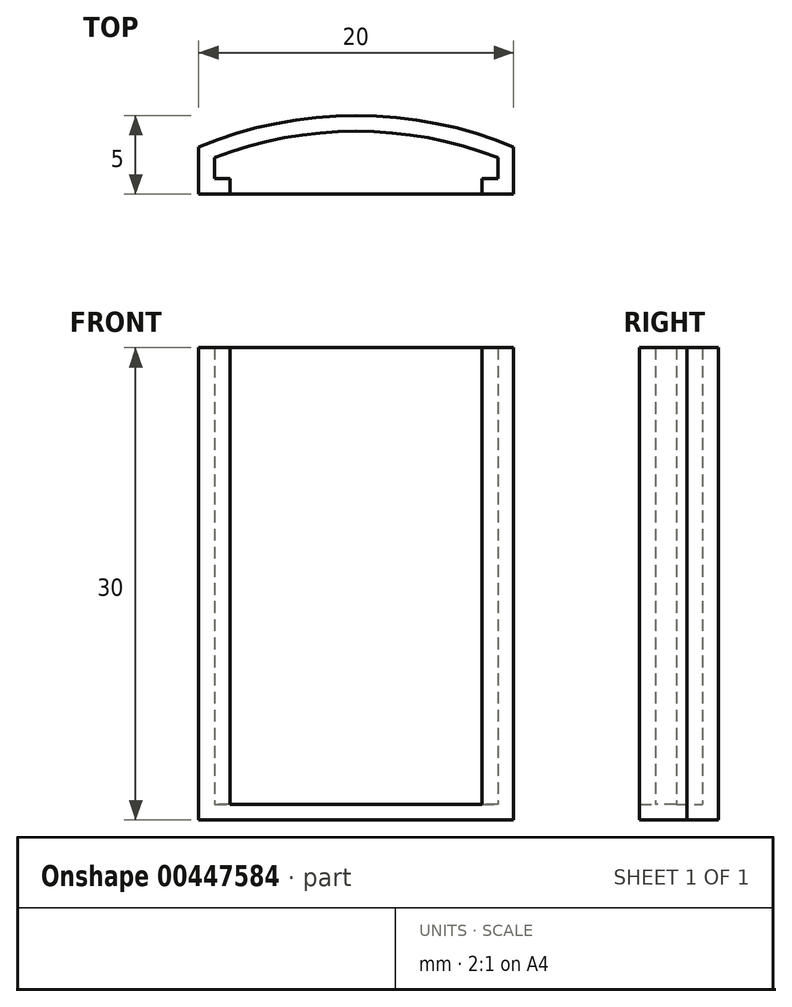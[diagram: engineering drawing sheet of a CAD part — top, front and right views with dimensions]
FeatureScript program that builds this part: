
annotation { "Feature Type Name" : "Feature", "Feature Type Description" : "" }
export const myFeature = defineFeature(function(context is Context, id is Id, definition is map)
    precondition{}
    {
        {
            var Q0;
            Q0=qCreatedBy(makeId("Top.planeOp"),FACE);
            var sketch = newSketch(context, id + "F0", { "sketchPlane" : qUnion([Q0])});
            skLineSegment(sketch, "E0.bottom", {"start": v(-10, 0) * mm, "end": v(-8, 0) * mm});
            skLineSegment(sketch, "E0.left", {"start": v(-10, 0) * mm, "end": v(-10, 3) * mm});
            skLineSegment(sketch, "E0.right", {"start": v(10, 0) * mm, "end": v(10, 3) * mm});
            skPoint(sketch, "E1.endSnap0", {"position": v(0, 5) * mm});
            skArc(sketch, "E2", {"start": v(10, 3) * mm, "mid": v(0, 5) * mm, "end": v(-10, 3) * mm});
            skLineSegment(sketch, "E3.0", {"start": v(-9, 1) * mm, "end": v(-9, 2.32) * mm});
            skArc(sketch, "E4.0", {"start": v(9, 2.32) * mm, "mid": v(0, 4) * mm, "end": v(-9, 2.32) * mm});
            skLineSegment(sketch, "E5.0", {"start": v(9, 1) * mm, "end": v(9, 2.32) * mm});
            skLineSegment(sketch, "E6.0", {"start": v(-9, 1) * mm, "end": v(-8, 1) * mm});
            skLineSegment(sketch, "E7", {"start": v(-8, 1) * mm, "end": v(-8, 0) * mm});
            skLineSegment(sketch, "E8", {"start": v(8, 1) * mm, "end": v(8, 0) * mm});
            skLineSegment(sketch, "E9.trimOffspring", {"start": v(8, 1) * mm, "end": v(9, 1) * mm});
            skLineSegment(sketch, "E10.trimOffspring", {"start": v(8, 0) * mm, "end": v(10, 0) * mm});
            skPoint(sketch, "E11.trimOffspring.end.orphan", {"position": v(0, -9) * mm});
            skPoint(sketch, "E1.start.orphan", {"position": v(0, 16.88) * mm});
            skSolve(sketch);
        }
        {
            var Q0;
            Q0=makeQuery(id+"F0.imprint","IMPRINT",FACE,{"disambiguationData":[TD([[makeQuery(id+"F0.imprint","IMPRINT",EDGE,{"derivedFrom":sQuery(id+"F0.wireOp",EDGE,"E0.bottom")}),1.0]])]});
            extrude(context, id + "F1", {"entities" : qUnion([Q0]), "depth" : 30 * mm});
        }
        {
            var Q0;
            Q0=makeQuery(id+"F1.opExtrude","CAP_FACE",FACE,{"disambiguationData":[OSD([sQuery(id+"F0.wireOp",EDGE,"E0.bottom"),sQuery(id+"F0.wireOp",EDGE,"E0.left"),sQuery(id+"F0.wireOp",EDGE,"E0.right"),sQuery(id+"F0.wireOp",EDGE,"E2"),sQuery(id+"F0.wireOp",EDGE,"E3.0"),sQuery(id+"F0.wireOp",EDGE,"E4.0"),sQuery(id+"F0.wireOp",EDGE,"E5.0"),sQuery(id+"F0.wireOp",EDGE,"E6.0"),sQuery(id+"F0.wireOp",EDGE,"E7"),sQuery(id+"F0.wireOp",EDGE,"E8"),sQuery(id+"F0.wireOp",EDGE,"E9.trimOffspring"),sQuery(id+"F0.wireOp",EDGE,"E10.trimOffspring")])],"isStart":true});
            var sketch = newSketch(context, id + "F2", { "sketchPlane" : qUnion([Q0])});
            skPoint(sketch, "E12.endSnap0", {"position": v(0, -5) * mm});
            skPoint(sketch, "E13.orphan", {"position": v(0, -6.47) * mm});
            skLineSegment(sketch, "E14", {"start": v(-10, 0) * mm, "end": v(-10, -3) * mm});
            skLineSegment(sketch, "E15", {"start": v(10, 0) * mm, "end": v(10, -3) * mm});
            skLineSegment(sketch, "E16", {"start": v(-10, 0) * mm, "end": v(10, 0) * mm});
            skArc(sketch, "E17", {"start": v(-10, -3) * mm, "mid": v(0, -5) * mm, "end": v(10, -3) * mm});
            skSolve(sketch);
        }
        {
            var Q0;
            Q0 = qSketchRegion(id + "F2", true);
            extrude(context, id + "F3", {"entities" : qUnion([Q0]), "operationType" : NewBodyOperationType.ADD, "oppositeDirection" : true, "depth" : 1 * mm});
        }
    });
